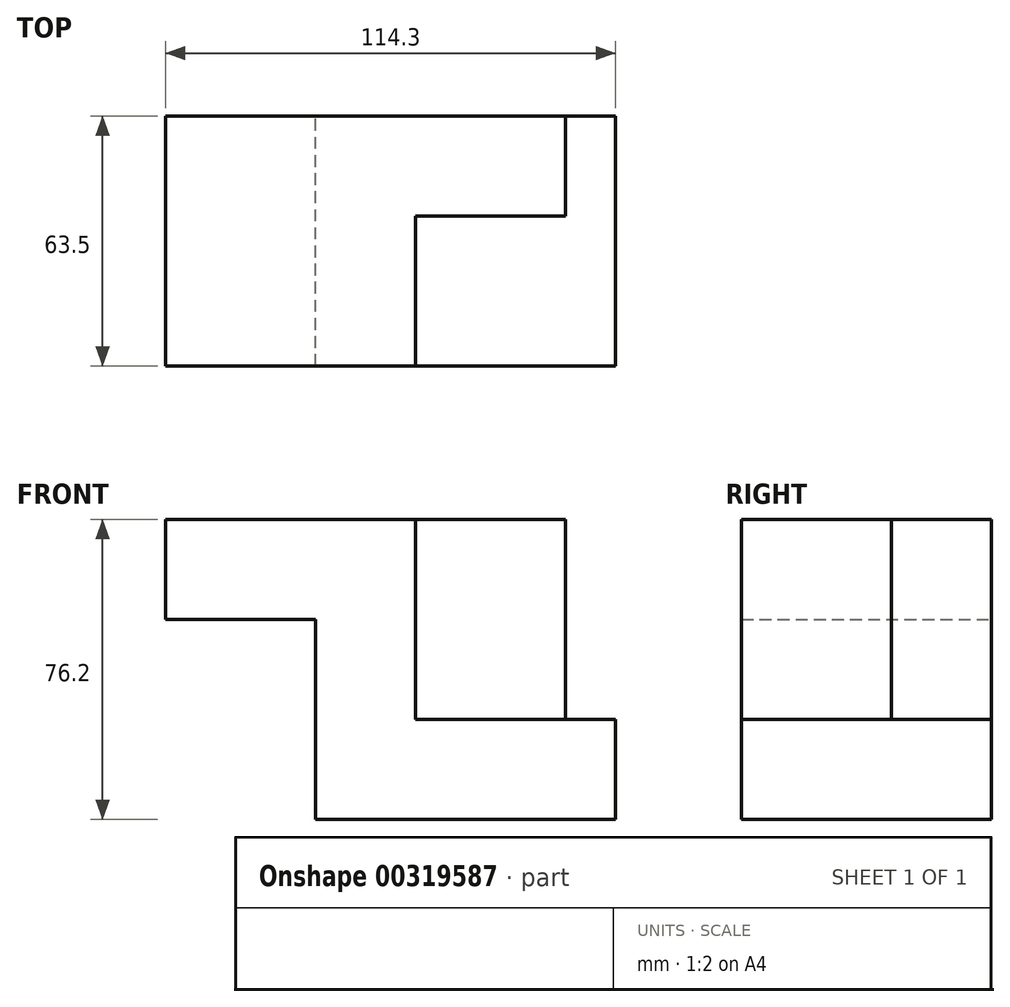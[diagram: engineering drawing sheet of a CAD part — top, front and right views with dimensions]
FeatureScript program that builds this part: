
annotation { "Feature Type Name" : "Feature", "Feature Type Description" : "" }
export const myFeature = defineFeature(function(context is Context, id is Id, definition is map)
    precondition{}
    {
        {
            var Q0;
            Q0=qCreatedBy(makeId("Front.planeOp"),FACE);
            var sketch = newSketch(context, id + "F0", { "sketchPlane" : qUnion([Q0])});
            skLineSegment(sketch, "E0", {"start": v(45.8, -50.8) * mm, "end": v(45.8, -25.4) * mm});
            skLineSegment(sketch, "E1", {"start": v(45.8, -25.4) * mm, "end": v(-5, -25.4) * mm});
            skLineSegment(sketch, "E2", {"start": v(-5, -25.4) * mm, "end": v(-5, 25.4) * mm});
            skLineSegment(sketch, "E3", {"start": v(-5, 25.4) * mm, "end": v(-68.5, 25.4) * mm});
            skLineSegment(sketch, "E4", {"start": v(-68.5, 25.4) * mm, "end": v(-68.5, 0) * mm});
            skLineSegment(sketch, "E5", {"start": v(-68.5, 0) * mm, "end": v(-30.4, 0) * mm});
            skLineSegment(sketch, "E6", {"start": v(-30.4, 0) * mm, "end": v(-30.4, -50.8) * mm});
            skLineSegment(sketch, "E7", {"start": v(-30.4, -50.8) * mm, "end": v(45.8, -50.8) * mm});
            skSolve(sketch);
        }
        {
            var Q0;
            Q0=makeQuery(id+"F0.imprint","IMPRINT",FACE,{"disambiguationData":[TD([[makeQuery(id+"F0.imprint","IMPRINT",EDGE,{"derivedFrom":sQuery(id+"F0.wireOp",EDGE,"UHq4b0Jt-e8vT-XE0B-eBBA-3Hntgs4YMbUQ")}),1.0]])]});
            var Q1;
            Q1=makeQuery(id+"F0.imprint","IMPRINT",FACE,{"disambiguationData":[TD([[makeQuery(id+"F0.imprint","IMPRINT",EDGE,{"derivedFrom":sQuery(id+"F0.wireOp",EDGE,"E0")}),1.0]])]});
            extrude(context, id + "F1", {"entities" : qUnion([Q0, Q1]), "depth" : 63.5 * mm});
        }
        {
            var Q0;
            Q0=makeQuery(id+"F1.opExtrude","SWEPT_FACE",FACE,{"disambiguationData":[OSD([sQuery(id+"F0.wireOp",EDGE,"E1")])]});
            var sketch = newSketch(context, id + "F2", { "sketchPlane" : qUnion([Q0])});
            skLineSegment(sketch, "E8", {"start": v(-5, 0) * mm, "end": v(-5, -25.4) * mm});
            skLineSegment(sketch, "E9", {"start": v(-5, -25.4) * mm, "end": v(33.1, -25.4) * mm});
            skLineSegment(sketch, "E10", {"start": v(33.1, -25.4) * mm, "end": v(33.1, 0) * mm});
            skLineSegment(sketch, "E11", {"start": v(33.1, 0) * mm, "end": v(-5, 0) * mm});
            skSolve(sketch);
        }
        {
            var Q0;
            Q0=makeQuery(id+"F2.imprint","IMPRINT",FACE,{"disambiguationData":[TD([[makeQuery(id+"F2.imprint","IMPRINT",EDGE,{"derivedFrom":sQuery(id+"F2.wireOp",EDGE,"E8")}),-1.0]])]});
            extrude(context, id + "F3", {"entities" : qUnion([Q0]), "operationType" : NewBodyOperationType.ADD, "depth" : 50.8 * mm});
        }
    });
